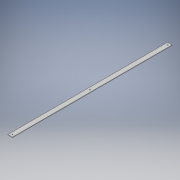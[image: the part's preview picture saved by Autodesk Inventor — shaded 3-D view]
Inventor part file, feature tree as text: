
AUTODESK INVENTOR PART (.ipt)
format: ipt  version: 2018 (Build 220112000, 112)  size: 107,008 bytes
history: native  units: in
note: dims shown in document units (in); Inventor stores cm internally (conversion verified against a paired STEP export)
features: extrude x2, sketch x2
ambient origin geometry x8: Origin, YZ Plane, XZ Plane, XY Plane, X Axis, Y Axis, Z Axis, Center Point
bodies: Solid1 (feature_tree)
feature tree (4):
  extrude  "Extrusion1"  Depth=0.125in
  extrude  "Extrusion2"  Depth=35.6554in
  sketch  "Sketch1"  dims[d0=1.0in d1=0.125in]
  sketch  "Sketch2"  dims[d2=35.6554in d3=0.0in d4=0.5in d5=0.5in d6=0.2031in d7=35.6554in d8=0.0in]
